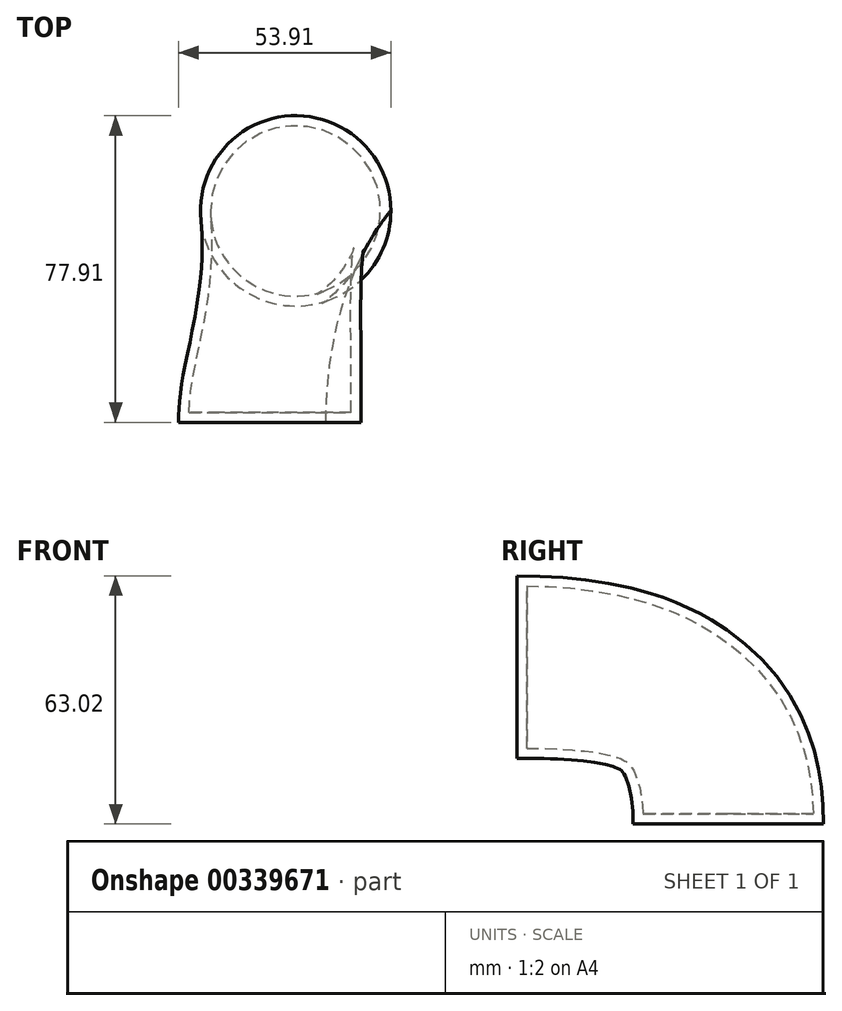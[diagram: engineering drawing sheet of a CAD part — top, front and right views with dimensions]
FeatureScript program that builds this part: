
annotation { "Feature Type Name" : "Feature", "Feature Type Description" : "" }
export const myFeature = defineFeature(function(context is Context, id is Id, definition is map)
    precondition{}
    {
        {
            var Q0;
            Q0=qCreatedBy(makeId("Top.planeOp"),FACE);
            var sketch = newSketch(context, id + "F0", { "sketchPlane" : qUnion([Q0])});
            skCircle(sketch, "E0", {"center": v(0, 53.73) * mm, "radius": 24.18 * mm});
            skSolve(sketch);
        }
        {
            var Q0;
            Q0=qCreatedBy(makeId("Front.planeOp"),FACE);
            var sketch = newSketch(context, id + "F1", { "sketchPlane" : qUnion([Q0])});
            skCircle(sketch, "E1", {"center": v(-6.55, 39.84) * mm, "radius": 23.17 * mm});
            skSolve(sketch);
        }
        {
            var Q0;
            Q0=makeQuery(id+"F0.imprint","IMPRINT",FACE,{"disambiguationData":[TD([[makeQuery(id+"F0.imprint","IMPRINT",EDGE,{"derivedFrom":sQuery(id+"F0.wireOp",EDGE,"E0")}),1.0]])]});
            var Q1;
            Q1=makeQuery(id+"F1.imprint","IMPRINT",FACE,{"disambiguationData":[TD([[makeQuery(id+"F1.imprint","IMPRINT",EDGE,{"derivedFrom":sQuery(id+"F1.wireOp",EDGE,"E1")}),1.0]])]});
            loft(context, id + "F2", {"startCondition" : LoftEndDerivativeType.NORMAL_TO_PROFILE, "startMagnitude" : 2, "endCondition" : LoftEndDerivativeType.NORMAL_TO_PROFILE, "endMagnitude" : 2, "sheetProfilesArray" : [{ "sheetProfileEntities" : qUnion([Q0]) }, { "sheetProfileEntities" : qUnion([Q1]) }]});
        }
        {
            var Q0;
            Q0=makeQuery(id+"F2.opLoft","SWEPT_FACE",FACE,{"disambiguationData":[OSD([sQuery(id+"F0.wireOp",EDGE,"E0"),sQuery(id+"F1.wireOp",EDGE,"E1")])]});
            var Q1;
            Q1=makeQuery(id+"F2.opLoft","SWEPT_BODY",BODY,{"disambiguationData":[OSD([makeQuery(id+"F0.imprint","IMPRINT",FACE,{"disambiguationData":[TD([[makeQuery(id+"F0.imprint","IMPRINT",EDGE,{"derivedFrom":sQuery(id+"F0.wireOp",EDGE,"E0")}),1.0]])]}),makeQuery(id+"F1.imprint","IMPRINT",FACE,{"disambiguationData":[TD([[makeQuery(id+"F1.imprint","IMPRINT",EDGE,{"derivedFrom":sQuery(id+"F1.wireOp",EDGE,"E1")}),1.0]])]})])]});
            shell(context, id + "F3", {"isHollow" : true, "entities" : qUnion([Q0]), "parts" : qUnion([Q1]), "thickness" : 2.54 * mm});
        }
    });
